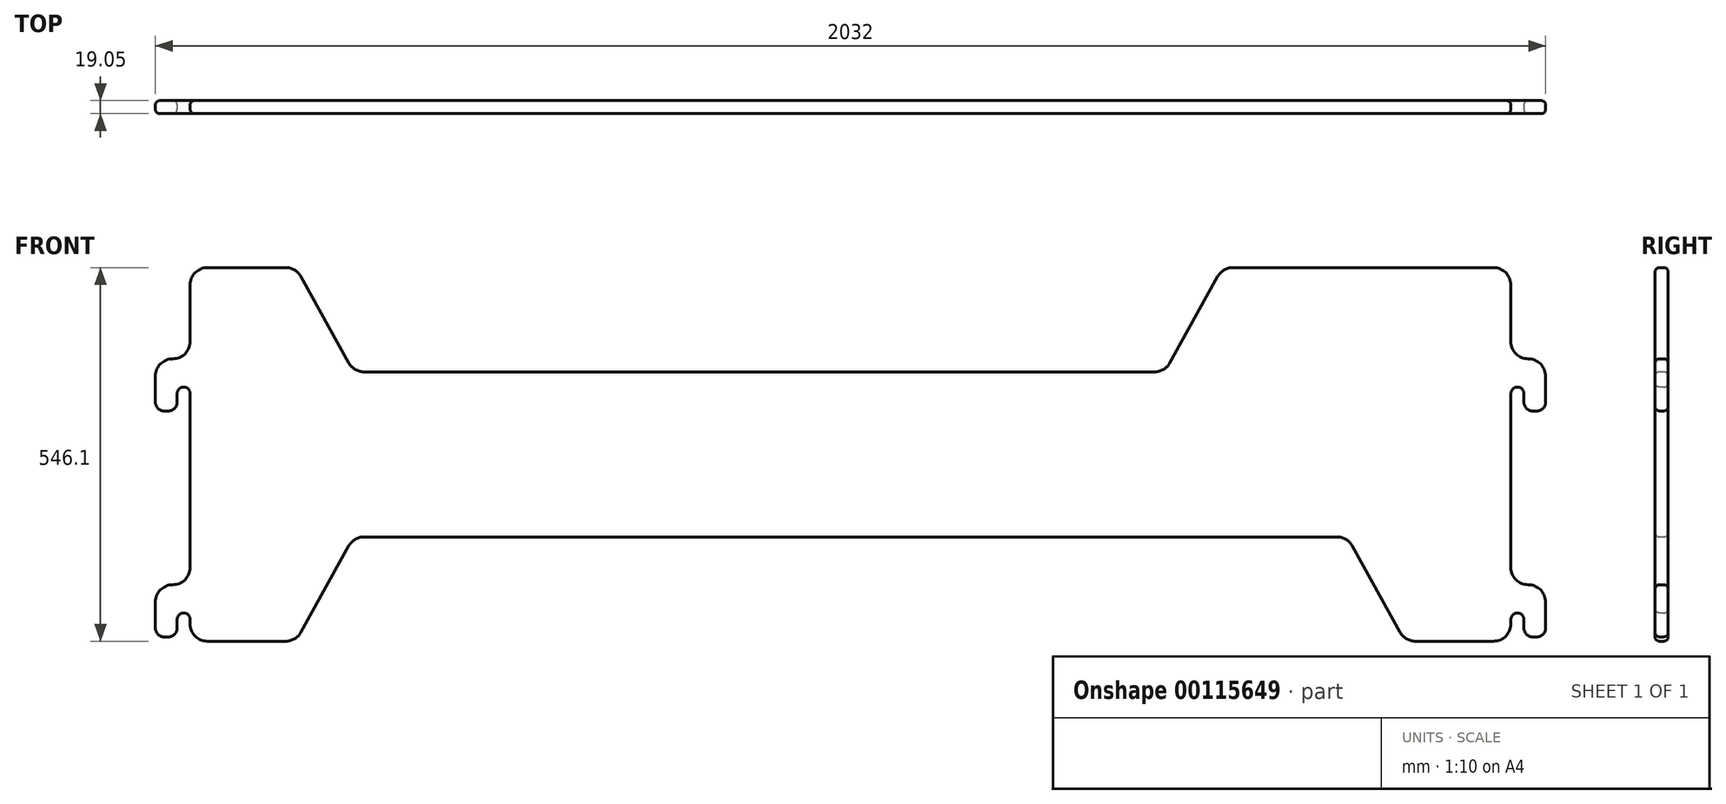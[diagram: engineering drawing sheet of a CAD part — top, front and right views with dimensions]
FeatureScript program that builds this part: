
annotation { "Feature Type Name" : "Feature", "Feature Type Description" : "" }
export const myFeature = defineFeature(function(context is Context, id is Id, definition is map)
    precondition{}
    {
        {
            var Q0;
            Q0=qCreatedBy(makeId("Front.planeOp"),FACE);
            var sketch = newSketch(context, id + "F0", { "sketchPlane" : qUnion([Q0])});
            skLineSegment(sketch, "E0.bottom", {"start": v(-965.2, 546.1) * mm, "end": v(-825.5, 546.1) * mm});
            skLineSegment(sketch, "E0.top", {"start": v(-965.2, 0) * mm, "end": v(-825.5, 0) * mm});
            skLineSegment(sketch, "E0.left", {"start": v(-965.2, 546.1) * mm, "end": v(-965.2, 0) * mm});
            skLineSegment(sketch, "E0.right", {"start": v(965.2, 546.1) * mm, "end": v(965.2, 0) * mm});
            skLineSegment(sketch, "E1", {"start": v(-803.28, 13.1) * mm, "end": v(-733.42, 139.3) * mm});
            skLineSegment(sketch, "E2", {"start": v(-711.2, 152.4) * mm, "end": v(711.2, 152.4) * mm});
            skLineSegment(sketch, "E3", {"start": v(733.42, 139.3) * mm, "end": v(803.28, 13.1) * mm});
            skLineSegment(sketch, "E4.trimOffspring", {"start": v(825.5, 0) * mm, "end": v(965.2, 0) * mm});
            skLineSegment(sketch, "E5", {"start": v(0, 546.1) * mm, "end": v(0, 0) * mm, "construction": true});
            skLineSegment(sketch, "E6", {"start": v(-803.28, 533) * mm, "end": v(-733.42, 406.8) * mm});
            skLineSegment(sketch, "E7", {"start": v(-711.2, 393.7) * mm, "end": v(444.5, 393.7) * mm});
            skLineSegment(sketch, "E8", {"start": v(466.72, 406.8) * mm, "end": v(536.58, 533) * mm});
            skLineSegment(sketch, "E9.trimOffspring", {"start": v(558.8, 546.1) * mm, "end": v(965.2, 546.1) * mm});
            skLineSegment(sketch, "E10", {"start": v(-965.2, 254) * mm, "end": v(965.2, 254) * mm, "construction": true});
            skLineSegment(sketch, "E11", {"start": v(965.2, 457.2) * mm, "end": v(-965.2, 457.2) * mm, "construction": true});
            skLineSegment(sketch, "E12", {"start": v(965.2, 412.75) * mm, "end": v(990.6, 412.75) * mm});
            skLineSegment(sketch, "E13", {"start": v(1016, 387.35) * mm, "end": v(1016, 349.25) * mm});
            skLineSegment(sketch, "E14", {"start": v(1003.3, 336.55) * mm, "end": v(996.95, 336.55) * mm});
            skLineSegment(sketch, "E15", {"start": v(984.25, 349.25) * mm, "end": v(984.25, 361.95) * mm});
            skArc(sketch, "E16", {"start": v(984.25, 361.95) * mm, "mid": v(974.73, 371.48) * mm, "end": v(965.2, 361.95) * mm});
            skArc(sketch, "E17", {"start": v(984.25, 31.75) * mm, "mid": v(974.73, 41.27) * mm, "end": v(965.2, 31.75) * mm});
            skLineSegment(sketch, "E18", {"start": v(984.25, 31.75) * mm, "end": v(984.25, 19.05) * mm});
            skLineSegment(sketch, "E19", {"start": v(996.95, 6.35) * mm, "end": v(1003.3, 6.35) * mm});
            skLineSegment(sketch, "E20", {"start": v(1016, 19.05) * mm, "end": v(1016, 57.15) * mm});
            skLineSegment(sketch, "E21", {"start": v(990.6, 82.55) * mm, "end": v(965.2, 82.55) * mm});
            skPoint(sketch, "E22.visualSharp", {"position": v(1016, 82.55) * mm});
            skArc(sketch, "E22.filletArc", {"start": v(1016, 57.15) * mm, "mid": v(1008.56, 75.11) * mm, "end": v(990.6, 82.55) * mm});
            skPoint(sketch, "E23.visualSharp", {"position": v(1016, 412.75) * mm});
            skArc(sketch, "E23.filletArc", {"start": v(1016, 387.35) * mm, "mid": v(1008.56, 405.31) * mm, "end": v(990.6, 412.75) * mm});
            skPoint(sketch, "E24.visualSharp", {"position": v(984.25, 336.55) * mm});
            skArc(sketch, "E24.filletArc", {"start": v(984.25, 349.25) * mm, "mid": v(987.97, 340.27) * mm, "end": v(996.95, 336.55) * mm});
            skPoint(sketch, "E25.visualSharp", {"position": v(1016, 336.55) * mm});
            skArc(sketch, "E25.filletArc", {"start": v(1003.3, 336.55) * mm, "mid": v(1012.28, 340.27) * mm, "end": v(1016, 349.25) * mm});
            skPoint(sketch, "E26.visualSharp", {"position": v(984.25, 6.35) * mm});
            skArc(sketch, "E26.filletArc", {"start": v(984.25, 19.05) * mm, "mid": v(987.97, 10.07) * mm, "end": v(996.95, 6.35) * mm});
            skPoint(sketch, "E27.visualSharp", {"position": v(1016, 6.35) * mm});
            skArc(sketch, "E27.filletArc", {"start": v(1003.3, 6.35) * mm, "mid": v(1012.28, 10.07) * mm, "end": v(1016, 19.05) * mm});
            skArc(sketch, "E28.MirrorCS", {"start": v(-1003.3, 336.55) * mm, "mid": v(-1012.28, 340.27) * mm, "end": v(-1016, 349.25) * mm});
            skLineSegment(sketch, "E29.MirrorCS", {"start": v(-1003.3, 336.55) * mm, "end": v(-996.95, 336.55) * mm});
            skLineSegment(sketch, "E30.MirrorCS", {"start": v(-984.25, 349.25) * mm, "end": v(-984.25, 361.95) * mm});
            skLineSegment(sketch, "E31.MirrorCS", {"start": v(-996.95, 6.35) * mm, "end": v(-1003.3, 6.35) * mm});
            skArc(sketch, "E32.MirrorCS", {"start": v(-984.25, 361.95) * mm, "mid": v(-974.73, 371.47) * mm, "end": v(-965.2, 361.95) * mm});
            skArc(sketch, "E33.MirrorCS", {"start": v(-984.25, 349.25) * mm, "mid": v(-987.97, 340.27) * mm, "end": v(-996.95, 336.55) * mm});
            skArc(sketch, "E34.MirrorCS", {"start": v(-984.25, 19.05) * mm, "mid": v(-987.97, 10.07) * mm, "end": v(-996.95, 6.35) * mm});
            skArc(sketch, "E35.MirrorCS", {"start": v(-984.25, 31.75) * mm, "mid": v(-974.73, 41.27) * mm, "end": v(-965.2, 31.75) * mm});
            skArc(sketch, "E36.MirrorCS", {"start": v(-1003.3, 6.35) * mm, "mid": v(-1012.28, 10.07) * mm, "end": v(-1016, 19.05) * mm});
            skLineSegment(sketch, "E37.MirrorCS", {"start": v(-984.25, 31.75) * mm, "end": v(-984.25, 19.05) * mm});
            skLineSegment(sketch, "E38.MirrorCS", {"start": v(-1016, 387.35) * mm, "end": v(-1016, 349.25) * mm});
            skArc(sketch, "E39.MirrorCS", {"start": v(-1016, 387.35) * mm, "mid": v(-1008.56, 405.31) * mm, "end": v(-990.6, 412.75) * mm});
            skArc(sketch, "E40.MirrorCS", {"start": v(-1016, 57.15) * mm, "mid": v(-1008.56, 75.11) * mm, "end": v(-990.6, 82.55) * mm});
            skLineSegment(sketch, "E41.MirrorCS", {"start": v(-1016, 19.05) * mm, "end": v(-1016, 57.15) * mm});
            skLineSegment(sketch, "E42.MirrorCS", {"start": v(-990.6, 82.55) * mm, "end": v(-965.2, 82.55) * mm});
            skLineSegment(sketch, "E43.MirrorCS", {"start": v(-965.2, 412.75) * mm, "end": v(-990.6, 412.75) * mm});
            skPoint(sketch, "E44.MirrorP", {"position": v(-1016, 6.35) * mm});
            skPoint(sketch, "E45.MirrorP", {"position": v(-1016, 82.55) * mm});
            skPoint(sketch, "E46.MirrorP", {"position": v(-1016, 412.75) * mm});
            skPoint(sketch, "E47.MirrorP", {"position": v(-1016, 336.55) * mm});
            skPoint(sketch, "E48.MirrorP", {"position": v(-984.25, 6.35) * mm});
            skPoint(sketch, "E49.MirrorP", {"position": v(-984.25, 336.55) * mm});
            skPoint(sketch, "E50.visualSharp", {"position": v(726.17, 152.4) * mm});
            skArc(sketch, "E50.filletArc", {"start": v(733.42, 139.3) * mm, "mid": v(724.1, 148.88) * mm, "end": v(711.2, 152.4) * mm});
            skPoint(sketch, "E51.visualSharp", {"position": v(810.53, 0) * mm});
            skArc(sketch, "E51.filletArc", {"start": v(803.28, 13.1) * mm, "mid": v(812.6, 3.52) * mm, "end": v(825.5, 0) * mm});
            skPoint(sketch, "E52.visualSharp", {"position": v(-810.53, 0) * mm});
            skArc(sketch, "E52.filletArc", {"start": v(-825.5, 0) * mm, "mid": v(-812.6, 3.52) * mm, "end": v(-803.28, 13.1) * mm});
            skPoint(sketch, "E53.visualSharp", {"position": v(-726.17, 152.4) * mm});
            skArc(sketch, "E53.filletArc", {"start": v(-711.2, 152.4) * mm, "mid": v(-724.1, 148.88) * mm, "end": v(-733.42, 139.3) * mm});
            skPoint(sketch, "E54.visualSharp", {"position": v(-810.53, 546.1) * mm});
            skArc(sketch, "E54.filletArc", {"start": v(-803.28, 533) * mm, "mid": v(-812.6, 542.58) * mm, "end": v(-825.5, 546.1) * mm});
            skPoint(sketch, "E55.visualSharp", {"position": v(-726.17, 393.7) * mm});
            skArc(sketch, "E55.filletArc", {"start": v(-733.42, 406.8) * mm, "mid": v(-724.1, 397.22) * mm, "end": v(-711.2, 393.7) * mm});
            skPoint(sketch, "E56.visualSharp", {"position": v(459.47, 393.7) * mm});
            skArc(sketch, "E56.filletArc", {"start": v(444.5, 393.7) * mm, "mid": v(457.4, 397.22) * mm, "end": v(466.72, 406.8) * mm});
            skPoint(sketch, "E57.visualSharp", {"position": v(543.83, 546.1) * mm});
            skArc(sketch, "E57.filletArc", {"start": v(558.8, 546.1) * mm, "mid": v(545.9, 542.58) * mm, "end": v(536.58, 533) * mm});
            skSolve(sketch);
        }
        {
            var Q0;
            Q0 = qSketchRegion(id + "F0", true);
            extrude(context, id + "F1", {"entities" : qUnion([Q0]), "oppositeDirection" : true, "depth" : 19.05 * mm});
        }
        {
            var Q0;
            Q0=makeQuery(id+"F1.opExtrude","SWEPT_EDGE",EDGE,{"disambiguationData":[OSD([sQuery(id+"F0.wireOp",EDGE,"E0.bottom"),sQuery(id+"F0.wireOp",EDGE,"E6")])]});
            var Q1;
            Q1=makeQuery(id+"F1.opExtrude","SWEPT_EDGE",EDGE,{"disambiguationData":[OSD([sQuery(id+"F0.wireOp",EDGE,"E6"),sQuery(id+"F0.wireOp",EDGE,"E7")])]});
            var Q2;
            Q2=makeQuery(id+"F1.opExtrude","SWEPT_EDGE",EDGE,{"disambiguationData":[OSD([sQuery(id+"F0.wireOp",EDGE,"E8"),sQuery(id+"F0.wireOp",EDGE,"E9.trimOffspring")])]});
            var Q3;
            Q3=makeQuery(id+"F1.opExtrude","SWEPT_EDGE",EDGE,{"disambiguationData":[OSD([sQuery(id+"F0.wireOp",EDGE,"E7"),sQuery(id+"F0.wireOp",EDGE,"E8")])]});
            var Q4;
            Q4=makeQuery(id+"F1.opExtrude","SWEPT_EDGE",EDGE,{"disambiguationData":[OSD([sQuery(id+"F0.wireOp",EDGE,"E2"),sQuery(id+"F0.wireOp",EDGE,"E3")])]});
            var Q5;
            Q5=makeQuery(id+"F1.opExtrude","SWEPT_EDGE",EDGE,{"disambiguationData":[OSD([sQuery(id+"F0.wireOp",EDGE,"E3"),sQuery(id+"F0.wireOp",EDGE,"E4.trimOffspring")])]});
            var Q6;
            Q6=makeQuery(id+"F1.opExtrude","SWEPT_EDGE",EDGE,{"disambiguationData":[OSD([sQuery(id+"F0.wireOp",EDGE,"E1"),sQuery(id+"F0.wireOp",EDGE,"E2")])]});
            var Q7;
            Q7=makeQuery(id+"F1.opExtrude","SWEPT_EDGE",EDGE,{"disambiguationData":[OSD([sQuery(id+"F0.wireOp",EDGE,"E0.top"),sQuery(id+"F0.wireOp",EDGE,"E1")])]});
            var Q8;
            Q8=makeQuery(id+"F1.opExtrude","SWEPT_EDGE",EDGE,{"disambiguationData":[OSD([sQuery(id+"F0.wireOp",EDGE,"E0.right"),sQuery(id+"F0.wireOp",EDGE,"E12")])]});
            var Q9;
            Q9=makeQuery(id+"F1.opExtrude","SWEPT_EDGE",EDGE,{"disambiguationData":[OSD([sQuery(id+"F0.wireOp",EDGE,"E0.right"),sQuery(id+"F0.wireOp",EDGE,"E21")])]});
            var Q10;
            Q10=makeQuery(id+"F1.opExtrude","SWEPT_EDGE",EDGE,{"disambiguationData":[OSD([sQuery(id+"F0.wireOp",EDGE,"E0.left"),sQuery(id+"F0.wireOp",EDGE,"E42.MirrorCS")])]});
            var Q11;
            Q11=makeQuery(id+"F1.opExtrude","SWEPT_EDGE",EDGE,{"disambiguationData":[OSD([sQuery(id+"F0.wireOp",EDGE,"E0.left"),sQuery(id+"F0.wireOp",EDGE,"E43.MirrorCS")])]});
            fillet(context, id + "F2", {"entities" : qUnion([Q0, Q1, Q2, Q3, Q4, Q5, Q6, Q7, Q8, Q9, Q10, Q11]), "radius" : 25.4 * mm, "tangentPropagation" : true, "allowEdgeOverflow" : false});
        }
        {
            var Q0;
            Q0=makeQuery(id+"F1.opExtrude","CAP_EDGE",EDGE,{"disambiguationData":[OSD([sQuery(id+"F0.wireOp",EDGE,"E7")])],"isStart":true});
            var Q1;
            Q1=makeQuery(id+"F1.opExtrude","CAP_EDGE",EDGE,{"disambiguationData":[OSD([sQuery(id+"F0.wireOp",EDGE,"E2")])],"isStart":true});
            var Q2;
            Q2=makeQuery(id+"F1.opExtrude","CAP_EDGE",EDGE,{"disambiguationData":[OSD([sQuery(id+"F0.wireOp",EDGE,"E7")])],"isStart":false});
            var Q3;
            Q3=makeQuery(id+"F1.opExtrude","CAP_EDGE",EDGE,{"disambiguationData":[OSD([sQuery(id+"F0.wireOp",EDGE,"E2")])],"isStart":false});
            var Q4;
            {var subQ0=sQuery(id+"F0.wireOp",EDGE,"E0.left");Q4=makeQuery(id+"F1.opExtrude","CAP_EDGE",EDGE,{"disambiguationData":[OSD([subQ0]),TDD([makeQuery(id+"F0.imprint","IMPRINT",EDGE,{"disambiguationData":[TD([[makeQuery(id+"F0.imprint","INTERSECT",VERTEX,{"derivedFrom":[subQ0,sQuery(id+"F0.wireOp",EDGE,"E32.MirrorCS")]}),-1.0]])],"derivedFrom":subQ0})])],"isStart":false});}
            var Q5;
            {var subQ0=sQuery(id+"F0.wireOp",EDGE,"E0.left");Q5=makeQuery(id+"F1.opExtrude","CAP_EDGE",EDGE,{"disambiguationData":[OSD([subQ0]),TDD([makeQuery(id+"F0.imprint","IMPRINT",EDGE,{"disambiguationData":[TD([[makeQuery(id+"F0.imprint","INTERSECT",VERTEX,{"derivedFrom":[subQ0,sQuery(id+"F0.wireOp",EDGE,"E32.MirrorCS")]}),-1.0]])],"derivedFrom":subQ0})])],"isStart":true});}
            var Q6;
            {var subQ0=sQuery(id+"F0.wireOp",EDGE,"E0.right");Q6=makeQuery(id+"F1.opExtrude","CAP_EDGE",EDGE,{"disambiguationData":[OSD([subQ0]),TDD([makeQuery(id+"F0.imprint","IMPRINT",EDGE,{"disambiguationData":[TD([[makeQuery(id+"F0.imprint","INTERSECT",VERTEX,{"derivedFrom":[subQ0,sQuery(id+"F0.wireOp",EDGE,"E16")]}),-1.0]])],"derivedFrom":subQ0})])],"isStart":true});}
            var Q7;
            {var subQ0=sQuery(id+"F0.wireOp",EDGE,"E0.right");Q7=makeQuery(id+"F1.opExtrude","CAP_EDGE",EDGE,{"disambiguationData":[OSD([subQ0]),TDD([makeQuery(id+"F0.imprint","IMPRINT",EDGE,{"disambiguationData":[TD([[makeQuery(id+"F0.imprint","INTERSECT",VERTEX,{"derivedFrom":[subQ0,sQuery(id+"F0.wireOp",EDGE,"E16")]}),-1.0]])],"derivedFrom":subQ0})])],"isStart":false});}
            fillet(context, id + "F3", {"entities" : qUnion([Q0, Q1, Q2, Q3, Q4, Q5, Q6, Q7]), "radius" : 6.35 * mm, "tangentPropagation" : true, "allowEdgeOverflow" : false});
        }
    });
